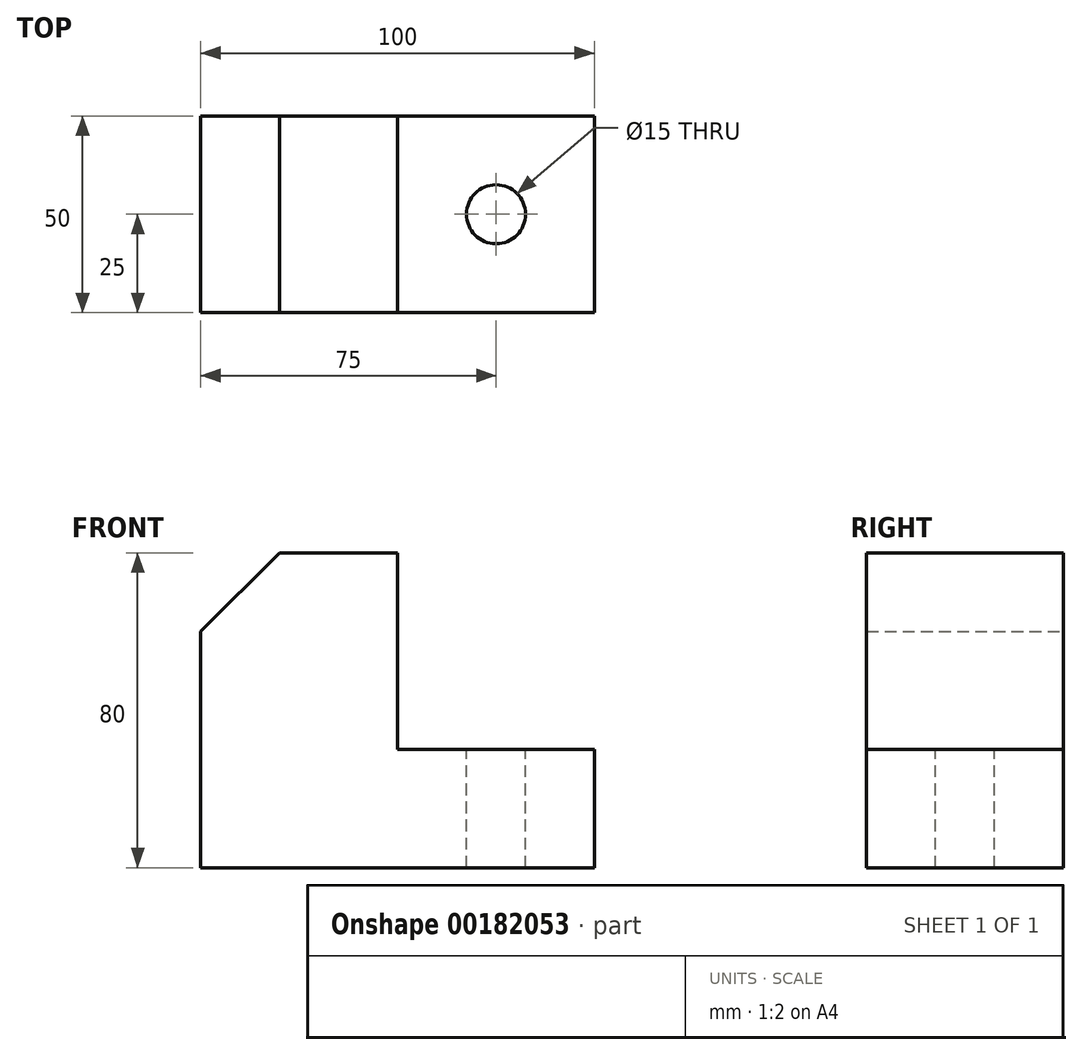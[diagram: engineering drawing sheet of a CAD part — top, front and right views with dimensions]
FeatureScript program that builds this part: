
annotation { "Feature Type Name" : "Feature", "Feature Type Description" : "" }
export const myFeature = defineFeature(function(context is Context, id is Id, definition is map)
    precondition{}
    {
        {
            var Q0;
            Q0=qCreatedBy(makeId("Front.planeOp"),FACE);
            var sketch = newSketch(context, id + "F0", { "sketchPlane" : qUnion([Q0])});
            skLineSegment(sketch, "E0", {"start": v(0, 0) * mm, "end": v(0, 80) * mm});
            skLineSegment(sketch, "E1", {"start": v(0, 80) * mm, "end": v(50, 80) * mm});
            skLineSegment(sketch, "E2", {"start": v(50, 80) * mm, "end": v(50, 30) * mm});
            skLineSegment(sketch, "E3", {"start": v(50, 30) * mm, "end": v(100, 30) * mm});
            skLineSegment(sketch, "E4", {"start": v(100, 30) * mm, "end": v(100, 0) * mm});
            skLineSegment(sketch, "E5", {"start": v(100, 0) * mm, "end": v(0, 0) * mm});
            skSolve(sketch);
        }
        {
            var Q0;
            Q0=makeQuery(id+"F0.imprint","IMPRINT",FACE,{"disambiguationData":[TD([[makeQuery(id+"F0.imprint","IMPRINT",EDGE,{"derivedFrom":sQuery(id+"F0.wireOp",EDGE,"E0")}),-1.0]])]});
            extrude(context, id + "F1", {"entities" : qUnion([Q0]), "depth" : 50 * mm});
        }
        {
            var Q0;
            Q0=makeQuery(id+"F1.opExtrude","SWEPT_FACE",FACE,{"disambiguationData":[OSD([sQuery(id+"F0.wireOp",EDGE,"E3")])]});
            var sketch = newSketch(context, id + "F2", { "sketchPlane" : qUnion([Q0])});
            skCircle(sketch, "E6", {"center": v(75, -25) * mm, "radius": 7.5 * mm});
            skSolve(sketch);
        }
        {
            var Q0;
            Q0 = qSketchRegion(id + "F2", true);
            extrude(context, id + "F3", {"entities" : qUnion([Q0]), "operationType" : NewBodyOperationType.REMOVE, "endBound" : BoundingType.THROUGH_ALL, "oppositeDirection" : true, "depth" : 25 * mm});
        }
        {
            var Q0;
            Q0=makeQuery(id+"F1.opExtrude","SWEPT_EDGE",EDGE,{"disambiguationData":[OSD([sQuery(id+"F0.wireOp",EDGE,"E0"),sQuery(id+"F0.wireOp",EDGE,"E1")])]});
            chamfer(context, id + "F4", {"entities" : qUnion([Q0]), "width" : 20 * mm, "tangentPropagation" : true});
        }
    });
